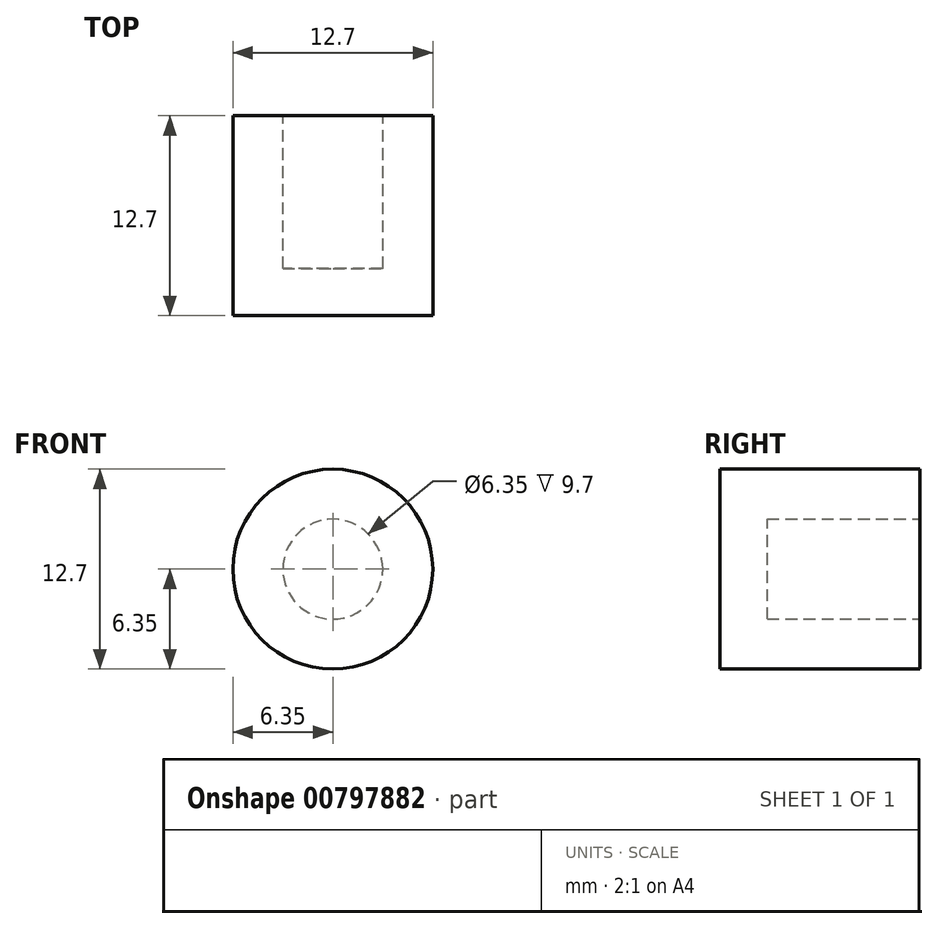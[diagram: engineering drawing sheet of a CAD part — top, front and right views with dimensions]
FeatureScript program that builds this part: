
annotation { "Feature Type Name" : "Feature", "Feature Type Description" : "" }
export const myFeature = defineFeature(function(context is Context, id is Id, definition is map)
    precondition{}
    {
        {
            var Q0;
            Q0=qCreatedBy(makeId("Front.planeOp"),FACE);
            var sketch = newSketch(context, id + "F0", { "sketchPlane" : qUnion([Q0])});
            skCircle(sketch, "E0", {"center": v(0, 0) * mm, "radius": 3.17 * mm});
            skCircle(sketch, "E1", {"center": v(0, 0) * mm, "radius": 6.35 * mm});
            skSolve(sketch);
        }
        {
            var Q0;
            Q0 = qSketchRegion(id + "F0", true);
            extrude(context, id + "F1", {"entities" : qUnion([Q0]), "depth" : 12.7 * mm, "offsetDistance" : 25 * mm});
        }
        {
            var Q0;
            Q0=makeQuery(id+"F1.opExtrude","CAP_FACE",FACE,{"disambiguationData":[OSD([sQuery(id+"F0.wireOp",EDGE,"E0"),sQuery(id+"F0.wireOp",EDGE,"E1")])],"isStart":false});
            var sketch = newSketch(context, id + "F2", { "sketchPlane" : qUnion([Q0])});
            skCircle(sketch, "E2", {"center": v(0, 0) * mm, "radius": 6.35 * mm});
            skSolve(sketch);
        }
        {
            var Q0;
            Q0 = qSketchRegion(id + "F2", true);
            extrude(context, id + "F3", {"entities" : qUnion([Q0]), "operationType" : NewBodyOperationType.ADD, "oppositeDirection" : true, "depth" : 3 * mm, "offsetDistance" : 25 * mm});
        }
    });
